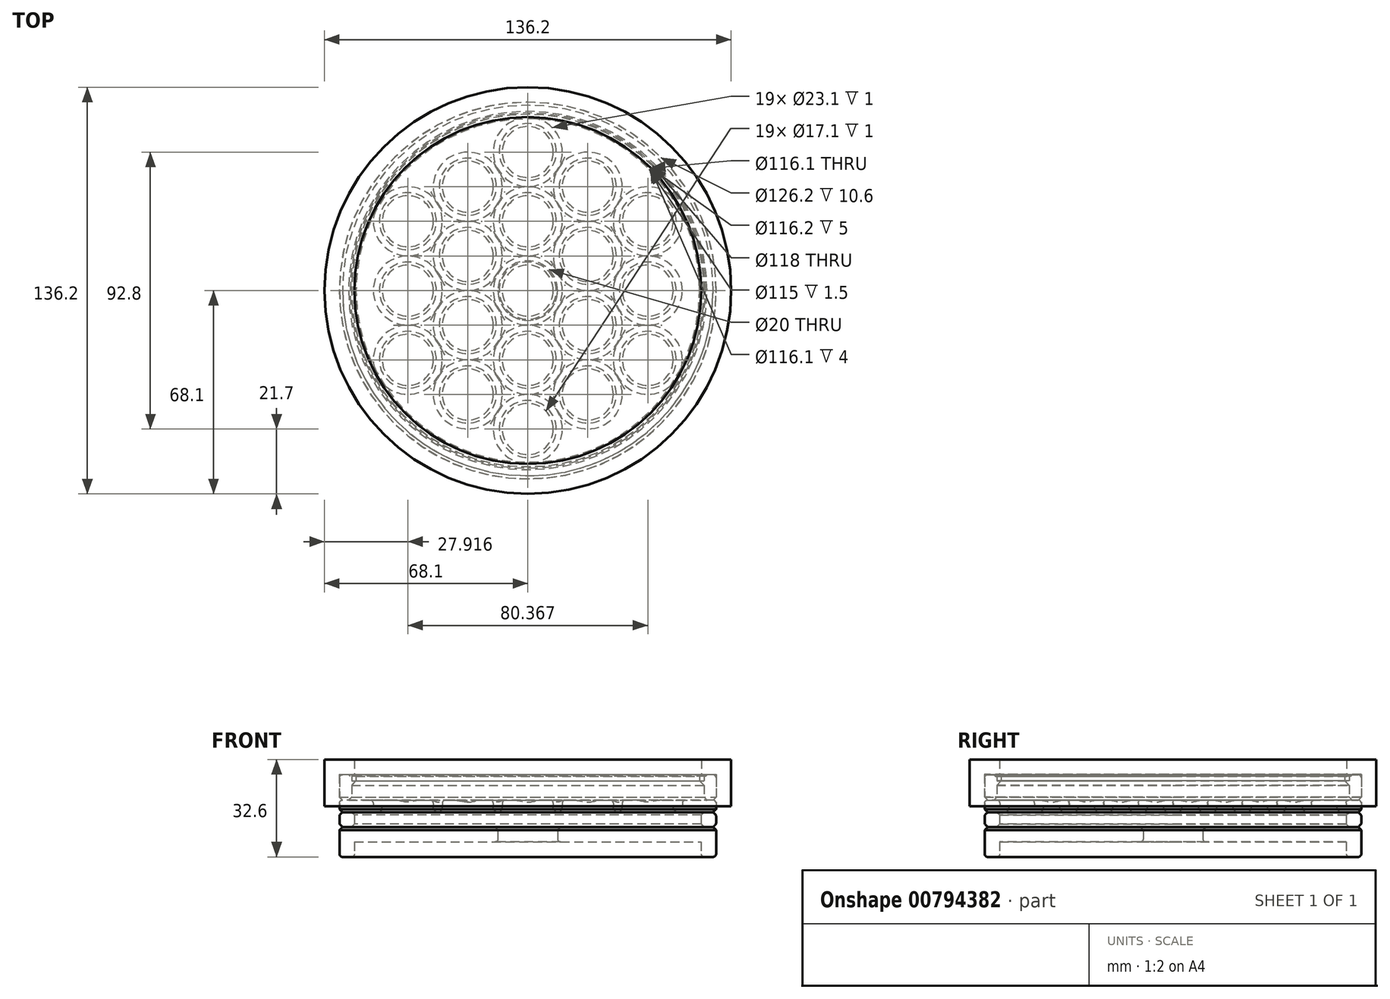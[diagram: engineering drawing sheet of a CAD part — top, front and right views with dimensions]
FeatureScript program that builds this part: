
annotation { "Feature Type Name" : "Feature", "Feature Type Description" : "" }
export const myFeature = defineFeature(function(context is Context, id is Id, definition is map)
    precondition{}
    {
        {
            var Q0;
            Q0=qCreatedBy(makeId("Top.planeOp"),FACE);
            var sketch = newSketch(context, id + "F0", { "sketchPlane" : qUnion([Q0])});
            skCircle(sketch, "E0", {"center": v(0, 0) * mm, "radius": 11.55 * mm});
            skCircle(sketch, "E1.0", {"center": v(0, 0) * mm, "radius": 11.65 * mm, "construction": true});
            skCircle(sketch, "E2.0.1.0", {"center": v(0, 23.2) * mm, "radius": 11.55 * mm});
            skCircle(sketch, "E2.0.2.0", {"center": v(0, 46.4) * mm, "radius": 11.55 * mm});
            skLineSegment(sketch, "E2.direction1", {"start": v(0, 0) * mm, "end": v(25, 0) * mm, "construction": true});
            skLineSegment(sketch, "E2.direction2", {"start": v(0, 0) * mm, "end": v(0, 23.2) * mm, "construction": true});
            skCircle(sketch, "E3.1.0", {"center": v(-20.1, 11.6) * mm, "radius": 11.55 * mm});
            skCircle(sketch, "E3.1.1", {"center": v(-40.18, 23.2) * mm, "radius": 11.55 * mm});
            skCircle(sketch, "E3.2.0", {"center": v(-20.1, -11.6) * mm, "radius": 11.55 * mm});
            skCircle(sketch, "E3.2.1", {"center": v(-40.18, -23.2) * mm, "radius": 11.55 * mm});
            skCircle(sketch, "E3.3.0", {"center": v(0, -23.2) * mm, "radius": 11.55 * mm});
            skCircle(sketch, "E3.3.1", {"center": v(0, -46.4) * mm, "radius": 11.55 * mm});
            skCircle(sketch, "E3.4.0", {"center": v(20.1, -11.6) * mm, "radius": 11.55 * mm});
            skCircle(sketch, "E3.4.1", {"center": v(40.18, -23.2) * mm, "radius": 11.55 * mm});
            skCircle(sketch, "E3.5.0", {"center": v(20.1, 11.6) * mm, "radius": 11.55 * mm});
            skCircle(sketch, "E3.5.1", {"center": v(40.18, 23.2) * mm, "radius": 11.55 * mm});
            skCircle(sketch, "E4.1.0.0", {"center": v(40.18, 0) * mm, "radius": 11.55 * mm});
            skLineSegment(sketch, "E4.direction1", {"start": v(0, 0) * mm, "end": v(40.18, 0) * mm, "construction": true});
            skCircle(sketch, "E5.0", {"center": v(40.18, 0) * mm, "radius": 11.65 * mm, "construction": true});
            skCircle(sketch, "E6.1.0", {"center": v(20.1, 34.8) * mm, "radius": 11.55 * mm});
            skCircle(sketch, "E6.2.0", {"center": v(-20.1, 34.8) * mm, "radius": 11.55 * mm});
            skCircle(sketch, "E6.3.0", {"center": v(-40.18, 0) * mm, "radius": 11.55 * mm});
            skCircle(sketch, "E6.4.0", {"center": v(-20.1, -34.8) * mm, "radius": 11.55 * mm});
            skCircle(sketch, "E6.5.0", {"center": v(20.1, -34.8) * mm, "radius": 11.55 * mm});
            skCircle(sketch, "E7.0", {"center": v(0, 0) * mm, "radius": 11.5 * mm, "construction": true});
            skSolve(sketch);
        }
        {
            var Q0;
            Q0=qCreatedBy(makeId("Top.planeOp"),FACE);
            var sketch = newSketch(context, id + "F1", { "sketchPlane" : qUnion([Q0])});
            skCircle(sketch, "E8.0", {"center": v(0, 0) * mm, "radius": 8.55 * mm});
            skCircle(sketch, "E9.0.1.0", {"center": v(0, 23.2) * mm, "radius": 8.55 * mm});
            skCircle(sketch, "E9.0.2.0", {"center": v(0, 46.4) * mm, "radius": 8.55 * mm});
            skLineSegment(sketch, "E9.direction1", {"start": v(0, 0) * mm, "end": v(25, 0) * mm, "construction": true});
            skLineSegment(sketch, "E9.direction2", {"start": v(0, 0) * mm, "end": v(0, 23.2) * mm, "construction": true});
            skCircle(sketch, "E10.1.0.0", {"center": v(40.18, 0) * mm, "radius": 8.55 * mm});
            skLineSegment(sketch, "E10.direction1", {"start": v(0, 0) * mm, "end": v(40.18, 0) * mm, "construction": true});
            skCircle(sketch, "E11.1.0", {"center": v(-20.1, 11.6) * mm, "radius": 8.55 * mm});
            skCircle(sketch, "E11.1.1", {"center": v(-40.18, 23.2) * mm, "radius": 8.55 * mm});
            skCircle(sketch, "E11.2.0", {"center": v(-20.1, -11.6) * mm, "radius": 8.55 * mm});
            skCircle(sketch, "E11.2.1", {"center": v(-40.18, -23.2) * mm, "radius": 8.55 * mm});
            skCircle(sketch, "E11.3.0", {"center": v(0, -23.2) * mm, "radius": 8.55 * mm});
            skCircle(sketch, "E11.3.1", {"center": v(0, -46.4) * mm, "radius": 8.55 * mm});
            skCircle(sketch, "E11.4.0", {"center": v(20.1, -11.6) * mm, "radius": 8.55 * mm});
            skCircle(sketch, "E11.4.1", {"center": v(40.18, -23.2) * mm, "radius": 8.55 * mm});
            skCircle(sketch, "E11.5.0", {"center": v(20.1, 11.6) * mm, "radius": 8.55 * mm});
            skCircle(sketch, "E11.5.1", {"center": v(40.18, 23.2) * mm, "radius": 8.55 * mm});
            skCircle(sketch, "E12.1.0", {"center": v(20.1, 34.8) * mm, "radius": 8.55 * mm});
            skCircle(sketch, "E12.2.0", {"center": v(-20.1, 34.8) * mm, "radius": 8.55 * mm});
            skCircle(sketch, "E12.3.0", {"center": v(-40.18, 0) * mm, "radius": 8.55 * mm});
            skCircle(sketch, "E12.4.0", {"center": v(-20.1, -34.8) * mm, "radius": 8.55 * mm});
            skCircle(sketch, "E12.5.0", {"center": v(20.1, -34.8) * mm, "radius": 8.55 * mm});
            skSolve(sketch);
        }
        {
            var Q0;
            Q0=qCreatedBy(makeId("Top.planeOp"),FACE);
            var sketch = newSketch(context, id + "F2", { "sketchPlane" : qUnion([Q0])});
            skCircle(sketch, "E13", {"center": v(0, 0) * mm, "radius": 63.05 * mm});
            skCircle(sketch, "E14.0", {"center": v(0, 46.4) * mm, "radius": 11.65 * mm, "construction": true});
            skCircle(sketch, "E15.0", {"center": v(0, 0) * mm, "radius": 58.05 * mm, "construction": true});
            skSolve(sketch);
        }
        {
            var Q0;
            Q0 = qSketchRegion(id + "F2", true);
            extrude(context, id + "F3", {"entities" : qUnion([Q0]), "endBound" : BoundingType.SYMMETRIC, "depth" : 4 * mm, "offsetDistance" : 25 * mm});
        }
        {
            var Q0;
            Q0 = qSketchRegion(id + "F0", true);
            extrude(context, id + "F4", {"entities" : qUnion([Q0]), "operationType" : NewBodyOperationType.REMOVE, "depth" : 2 * mm, "offsetDistance" : 25 * mm});
        }
        {
            var Q0;
            Q0 = qSketchRegion(id + "F1", true);
            extrude(context, id + "F5", {"entities" : qUnion([Q0]), "operationType" : NewBodyOperationType.REMOVE, "oppositeDirection" : true, "depth" : 2 * mm, "offsetDistance" : 25 * mm});
        }
        {
            var Q0;
            Q0=makeQuery(id+"F3.opExtrude","CAP_FACE",FACE,{"disambiguationData":[OSD([sQuery(id+"F2.wireOp",EDGE,"E13")])],"isStart":true});
            chamfer(context, id + "F6", {"entities" : qUnion([Q0]), "width" : 1 * mm, "tangentPropagation" : true});
        }
        {
            var Q0;
            Q0=makeQuery(id+"F3.opExtrude","CAP_FACE",FACE,{"disambiguationData":[OSD([sQuery(id+"F2.wireOp",EDGE,"E13")])],"isStart":false});
            fillet(context, id + "F7", {"entities" : qUnion([Q0]), "radius" : 1 * mm, "tangentPropagation" : true, "allowEdgeOverflow" : false});
        }
        {
            var Q0;
            Q0=qCreatedBy(makeId("Front.planeOp"),FACE);
            var sketch = newSketch(context, id + "F8", { "sketchPlane" : qUnion([Q0])});
            skLineSegment(sketch, "E16", {"start": v(-57.5, 10.5) * mm, "end": v(-57.5, 0) * mm, "construction": true});
            skLineSegment(sketch, "E17", {"start": v(-63.05, 0) * mm, "end": v(63.05, 0) * mm, "construction": true});
            skLineSegment(sketch, "E18", {"start": v(-63.05, 2) * mm, "end": v(-63.05, 10.5) * mm});
            skLineSegment(sketch, "E19", {"start": v(-63.05, 10.5) * mm, "end": v(-59, 10.5) * mm});
            skLineSegment(sketch, "E20", {"start": v(-59, 10.5) * mm, "end": v(-59, 8.5) * mm});
            skLineSegment(sketch, "E21", {"start": v(-59, 8.5) * mm, "end": v(-57.5, 8.5) * mm});
            skLineSegment(sketch, "E22", {"start": v(-57.5, 8.5) * mm, "end": v(-59, 7) * mm});
            skLineSegment(sketch, "E23", {"start": v(-59, 7) * mm, "end": v(-59, 2) * mm});
            skLineSegment(sketch, "E24", {"start": v(-59, 2) * mm, "end": v(-63.05, 2) * mm});
            skLineSegment(sketch, "E25.0", {"start": v(-59, 8.5) * mm, "end": v(59, 8.5) * mm, "construction": true});
            skLineSegment(sketch, "E25.1", {"start": v(-59, 10.5) * mm, "end": v(-59, 8.5) * mm, "construction": true});
            skLineSegment(sketch, "E26", {"start": v(0, 0) * mm, "end": v(0, 8.5) * mm, "construction": true});
            skLineSegment(sketch, "E27", {"start": v(-59, 10) * mm, "end": v(-57.5, 10) * mm});
            skLineSegment(sketch, "E28", {"start": v(-57.5, 10) * mm, "end": v(-57.5, 8.5) * mm});
            skSolve(sketch);
        }
        {
            var Q0;
            Q0=qCreatedBy(makeId("Front.planeOp"),FACE);
            var sketch = newSketch(context, id + "F9", { "sketchPlane" : qUnion([Q0])});
            skLineSegment(sketch, "E29.bottom", {"start": v(0, 8.5) * mm, "end": v(-59, 8.5) * mm});
            skLineSegment(sketch, "E29.top", {"start": v(0, 10.5) * mm, "end": v(-59, 10.5) * mm});
            skLineSegment(sketch, "E29.left", {"start": v(0, 8.5) * mm, "end": v(0, 10.5) * mm});
            skLineSegment(sketch, "E29.right", {"start": v(-59, 8.5) * mm, "end": v(-59, 10.5) * mm});
            skSolve(sketch);
        }
        {
            var Q0;
            Q0 = qSketchRegion(id + "F8", true);
            var Q1;
            Q1 = qSketchRegion(id + "F9", true);
            var Q2;
            Q2=sQuery(id+"F9.wireOp",EDGE,"E29.left");
            revolve(context, id + "F10", {"surfaceOperationType" : NewSurfaceOperationType.NEW, "entities" : qUnion([Q0, Q1]), "axis" : qUnion([Q2]), "revolveType" : RevolveType.FULL});
        }
        {
            var Q0;
            Q0=makeQuery(id+"F10.opRevolve","SWEPT_EDGE",EDGE,{"disambiguationData":[OSD([sQuery(id+"F8.wireOp",EDGE,"E18"),sQuery(id+"F8.wireOp",EDGE,"E24")])]});
            var Q1;
            Q1=makeQuery(id+"F10.opRevolve","SWEPT_EDGE",EDGE,{"disambiguationData":[OSD([sQuery(id+"F8.wireOp",EDGE,"E23"),sQuery(id+"F8.wireOp",EDGE,"E24")])]});
            var Q2;
            Q2=makeQuery(id+"F10.opRevolve","SWEPT_EDGE",EDGE,{"disambiguationData":[OSD([sQuery(id+"F8.wireOp",EDGE,"E19"),sQuery(id+"F8.wireOp",EDGE,"E20")])]});
            chamfer(context, id + "F11", {"entities" : qUnion([Q0, Q1, Q2]), "width" : 1 * mm, "tangentPropagation" : true});
        }
        {
            var Q0;
            Q0=makeQuery(id+"F10.opRevolve","SWEPT_EDGE",EDGE,{"disambiguationData":[OSD([sQuery(id+"F8.wireOp",EDGE,"E18"),sQuery(id+"F8.wireOp",EDGE,"E19")])]});
            fillet(context, id + "F12", {"entities" : qUnion([Q0]), "radius" : 1 * mm, "tangentPropagation" : true, "allowEdgeOverflow" : false});
        }
        {
            var Q0;
            Q0=qCreatedBy(makeId("Right.planeOp"),FACE);
            var sketch = newSketch(context, id + "F13", { "sketchPlane" : qUnion([Q0])});
            skLineSegment(sketch, "E30", {"start": v(-63.1, 0) * mm, "end": v(-63.1, 10.6) * mm});
            skLineSegment(sketch, "E31", {"start": v(-63.1, 10.6) * mm, "end": v(-58.1, 10.6) * mm});
            skLineSegment(sketch, "E32", {"start": v(-58.1, 10.6) * mm, "end": v(-58.1, 15.6) * mm});
            skLineSegment(sketch, "E33", {"start": v(-58.1, 15.6) * mm, "end": v(-68.1, 15.6) * mm});
            skLineSegment(sketch, "E34", {"start": v(-68.1, 15.6) * mm, "end": v(-68.1, 0) * mm});
            skLineSegment(sketch, "E35", {"start": v(-68.1, 0) * mm, "end": v(-63.1, 0) * mm});
            skLineSegment(sketch, "E36", {"start": v(-63.05, 0) * mm, "end": v(63.05, 0) * mm, "construction": true});
            skSolve(sketch);
        }
        {
            var Q0;
            Q0 = qSketchRegion(id + "F13", true);
            var Q1;
            {var subQ0=sQuery(id+"F8.wireOp",EDGE,"E18");Q1=makeQuery(id+"F12.opFillet","BLEND_EDGE",EDGE,{"blendedFrom":[makeQuery(id+"F10.opRevolve","SWEPT_EDGE",EDGE,{"disambiguationData":[OSD([subQ0,sQuery(id+"F8.wireOp",EDGE,"E19")])]}),makeQuery(id+"F10.opRevolve","SWEPT_FACE",FACE,{"disambiguationData":[OSD([subQ0])]})],"blendedInto":[makeQuery(id+"F10.opRevolve","SWEPT_FACE",FACE,{"disambiguationData":[OSD([subQ0])]})]});}
            revolve(context, id + "F14", {"surfaceOperationType" : NewSurfaceOperationType.NEW, "entities" : qUnion([Q0]), "axis" : qUnion([Q1]), "revolveType" : RevolveType.FULL});
        }
        {
            var Q0;
            Q0=qCreatedBy(makeId("Front.planeOp"),FACE);
            var sketch = newSketch(context, id + "F15", { "sketchPlane" : qUnion([Q0])});
            skLineSegment(sketch, "E37.bottom", {"start": v(-63.05, -2) * mm, "end": v(-58.05, -2) * mm});
            skLineSegment(sketch, "E37.top", {"start": v(-63.05, -7) * mm, "end": v(-58.05, -7) * mm});
            skLineSegment(sketch, "E37.left", {"start": v(-63.05, -2) * mm, "end": v(-63.05, -7) * mm});
            skLineSegment(sketch, "E37.right", {"start": v(-58.05, -2) * mm, "end": v(-58.05, -7) * mm});
            skLineSegment(sketch, "E38", {"start": v(-63.05, 0) * mm, "end": v(63.05, 0) * mm});
            skSolve(sketch);
        }
        {
            var Q0;
            Q0 = qSketchRegion(id + "F15", true);
            var Q1;
            {var subQ0=sQuery(id+"F2.wireOp",EDGE,"E13");Q1=makeQuery(id+"F6.opChamfer","BLEND_EDGE",EDGE,{"blendedFrom":[makeQuery(id+"F3.opExtrude","CAP_EDGE",EDGE,{"disambiguationData":[OSD([subQ0])],"isStart":true}),makeQuery(id+"F3.opExtrude","CAP_FACE",FACE,{"disambiguationData":[OSD([subQ0])],"isStart":true})],"blendedInto":[makeQuery(id+"F3.opExtrude","CAP_FACE",FACE,{"disambiguationData":[OSD([subQ0])],"isStart":true})]});}
            revolve(context, id + "F16", {"surfaceOperationType" : NewSurfaceOperationType.NEW, "entities" : qUnion([Q0]), "axis" : qUnion([Q1]), "revolveType" : RevolveType.FULL});
        }
        {
            var Q0;
            Q0=qCreatedBy(makeId("Front.planeOp"),FACE);
            var sketch = newSketch(context, id + "F17", { "sketchPlane" : qUnion([Q0])});
            skLineSegment(sketch, "E39", {"start": v(-63.05, -7) * mm, "end": v(-63.05, -17) * mm});
            skLineSegment(sketch, "E40", {"start": v(-63.05, -17) * mm, "end": v(-58.05, -17) * mm});
            skLineSegment(sketch, "E41", {"start": v(-58.05, -17) * mm, "end": v(-58.05, -12) * mm});
            skLineSegment(sketch, "E42", {"start": v(-58.05, -12) * mm, "end": v(0, -12) * mm});
            skLineSegment(sketch, "E43", {"start": v(0, -12) * mm, "end": v(0, -7) * mm});
            skLineSegment(sketch, "E44", {"start": v(0, -7) * mm, "end": v(-63.05, -7) * mm});
            skLineSegment(sketch, "E45", {"start": v(-63.05, 0) * mm, "end": v(63.05, 0) * mm, "construction": true});
            skLineSegment(sketch, "E46", {"start": v(-10, -12) * mm, "end": v(-10, -7) * mm});
            skSolve(sketch);
        }
        {
            var Q0;
            {var subQ3=sQuery(id+"F17.wireOp",EDGE,"E39");Q0=makeQuery(id+"F17.imprint","IMPRINT",FACE,{"disambiguationData":[TD([[makeQuery(id+"F17.imprint","IMPRINT",EDGE,{"derivedFrom":subQ3}),1.0]])]});}
            var Q1;
            Q1=sQuery(id+"F17.wireOp",EDGE,"E43");
            revolve(context, id + "F18", {"surfaceOperationType" : NewSurfaceOperationType.NEW, "entities" : qUnion([Q0]), "axis" : qUnion([Q1]), "revolveType" : RevolveType.FULL});
        }
        {
            var Q0;
            Q0=makeQuery(id+"F16.opRevolve","SWEPT_FACE",FACE,{"disambiguationData":[OSD([sQuery(id+"F15.wireOp",EDGE,"E37.bottom")])]});
            var Q1;
            Q1=makeQuery(id+"F16.opRevolve","SWEPT_FACE",FACE,{"disambiguationData":[OSD([sQuery(id+"F15.wireOp",EDGE,"E37.top")])]});
            chamfer(context, id + "F19", {"entities" : qUnion([Q0, Q1]), "width" : 1 * mm, "tangentPropagation" : true});
        }
        {
            var Q0;
            {var subQ0=sQuery(id+"F15.wireOp",EDGE,"E37.left");Q0=makeQuery(id+"F19.opChamfer","BLEND_EDGE",EDGE,{"blendedFrom":[makeQuery(id+"F16.opRevolve","SWEPT_EDGE",EDGE,{"disambiguationData":[OSD([sQuery(id+"F15.wireOp",EDGE,"E37.top"),subQ0])]}),makeQuery(id+"F16.opRevolve","SWEPT_FACE",FACE,{"disambiguationData":[OSD([subQ0])]})],"blendedInto":[makeQuery(id+"F16.opRevolve","SWEPT_FACE",FACE,{"disambiguationData":[OSD([subQ0])]})]});}
            var Q1;
            {var subQ0=sQuery(id+"F15.wireOp",EDGE,"E37.left");Q1=makeQuery(id+"F19.opChamfer","BLEND_EDGE",EDGE,{"blendedFrom":[makeQuery(id+"F16.opRevolve","SWEPT_EDGE",EDGE,{"disambiguationData":[OSD([sQuery(id+"F15.wireOp",EDGE,"E37.bottom"),subQ0])]}),makeQuery(id+"F16.opRevolve","SWEPT_FACE",FACE,{"disambiguationData":[OSD([subQ0])]})],"blendedInto":[makeQuery(id+"F16.opRevolve","SWEPT_FACE",FACE,{"disambiguationData":[OSD([subQ0])]})]});}
            fillet(context, id + "F20", {"entities" : qUnion([Q0, Q1]), "radius" : 1 * mm, "tangentPropagation" : true, "allowEdgeOverflow" : false});
        }
        {
            var Q0;
            Q0=makeQuery(id+"F18.opRevolve","SWEPT_FACE",FACE,{"disambiguationData":[OSD([sQuery(id+"F17.wireOp",EDGE,"E44")])]});
            chamfer(context, id + "F21", {"entities" : qUnion([Q0]), "width" : 1 * mm, "tangentPropagation" : true});
        }
        {
            var Q0;
            Q0=makeQuery(id+"F18.opRevolve","SWEPT_FACE",FACE,{"disambiguationData":[OSD([sQuery(id+"F17.wireOp",EDGE,"E40")])]});
            var Q1;
            Q1=makeQuery(id+"F18.opRevolve","SWEPT_EDGE",EDGE,{"disambiguationData":[OSD([sQuery(id+"F17.wireOp",EDGE,"E42"),sQuery(id+"F17.wireOp",EDGE,"E46")])]});
            var Q2;
            {var subQ0=sQuery(id+"F17.wireOp",EDGE,"E46");Q2=makeQuery(id+"F21.opChamfer","BLEND_EDGE",EDGE,{"blendedFrom":[makeQuery(id+"F18.opRevolve","SWEPT_EDGE",EDGE,{"disambiguationData":[OSD([sQuery(id+"F17.wireOp",EDGE,"E44"),subQ0])]}),makeQuery(id+"F18.opRevolve","SWEPT_FACE",FACE,{"disambiguationData":[OSD([subQ0])]})],"blendedInto":[makeQuery(id+"F18.opRevolve","SWEPT_FACE",FACE,{"disambiguationData":[OSD([subQ0])]})]});}
            var Q3;
            {var subQ0=sQuery(id+"F17.wireOp",EDGE,"E44");Q3=makeQuery(id+"F21.opChamfer","BLEND_EDGE",EDGE,{"blendedFrom":[makeQuery(id+"F18.opRevolve","SWEPT_EDGE",EDGE,{"disambiguationData":[OSD([subQ0,sQuery(id+"F17.wireOp",EDGE,"E46")])]}),makeQuery(id+"F18.opRevolve","SWEPT_FACE",FACE,{"disambiguationData":[OSD([subQ0])]})],"blendedInto":[makeQuery(id+"F18.opRevolve","SWEPT_FACE",FACE,{"disambiguationData":[OSD([subQ0])]})]});}
            fillet(context, id + "F22", {"entities" : qUnion([Q0, Q1, Q2, Q3]), "radius" : 1 * mm, "tangentPropagation" : true, "allowEdgeOverflow" : false});
        }
    });
